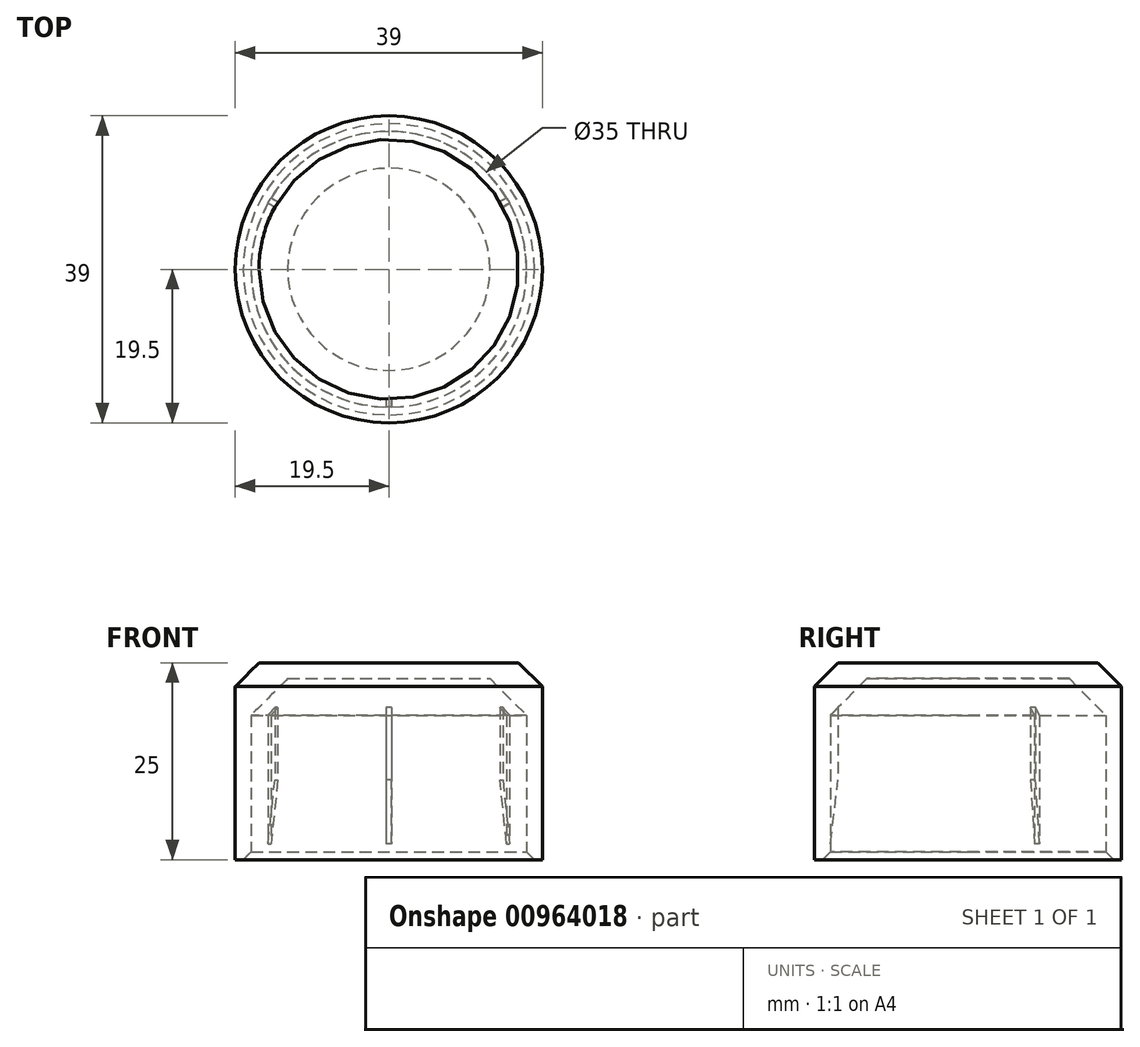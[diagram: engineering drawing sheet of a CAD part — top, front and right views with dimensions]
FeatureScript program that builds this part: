
annotation { "Feature Type Name" : "Feature", "Feature Type Description" : "" }
export const myFeature = defineFeature(function(context is Context, id is Id, definition is map)
    precondition{}
    {
        {
            var Q0;
            Q0=qCreatedBy(makeId("Front.planeOp"),FACE);
            var sketch = newSketch(context, id + "F0", { "sketchPlane" : qUnion([Q0])});
            skLineSegment(sketch, "E0", {"start": v(0, 0) * mm, "end": v(0, 33.94) * mm, "construction": true});
            skLineSegment(sketch, "E1", {"start": v(0, 25) * mm, "end": v(16.5, 25) * mm});
            skLineSegment(sketch, "E2", {"start": v(19.5, 22) * mm, "end": v(19.5, 0) * mm});
            skLineSegment(sketch, "E3", {"start": v(19.5, 0) * mm, "end": v(18.5, 0) * mm});
            skLineSegment(sketch, "E4", {"start": v(18.5, 0) * mm, "end": v(17.5, 1) * mm});
            skLineSegment(sketch, "E5", {"start": v(17.5, 1) * mm, "end": v(17.5, 18.34) * mm});
            skLineSegment(sketch, "E6", {"start": v(12.84, 23) * mm, "end": v(0, 23) * mm});
            skLineSegment(sketch, "E7", {"start": v(0, 23) * mm, "end": v(0, 25) * mm});
            skLineSegment(sketch, "E8", {"start": v(12.84, 23) * mm, "end": v(17.5, 18.34) * mm});
            skLineSegment(sketch, "E9", {"start": v(16.5, 25) * mm, "end": v(19.5, 22) * mm});
            skLineSegment(sketch, "E10", {"start": v(17.5, 1) * mm, "end": v(19.5, 1) * mm, "construction": true});
            skSolve(sketch);
        }
        {
            var Q0;
            Q0 = qSketchRegion(id + "F0", true);
            var Q1;
            Q1=sQuery(id+"F0.wireOp",EDGE,"E0");
            revolve(context, id + "F1", {"surfaceOperationType" : NewSurfaceOperationType.NEW, "entities" : qUnion([Q0]), "axis" : qUnion([Q1]), "revolveType" : RevolveType.FULL});
        }
        {
            var Q0;
            Q0=qCreatedBy(makeId("Top.planeOp"),FACE);
            cPlane(context, id + "F2", {"entities" : qUnion([Q0]), "cplaneType" : CPlaneType.OFFSET, "offset" : 2 * mm, "width" : 150 * mm, "height" : 150 * mm});
        }
        {
            var Q0;
            Q0=qCreatedBy(id+"F2.planeOp",FACE);
            var sketch = newSketch(context, id + "F3", { "sketchPlane" : qUnion([Q0])});
            skLineSegment(sketch, "E11.bottom", {"start": v(-0.38, -18.5) * mm, "end": v(0.38, -18.5) * mm});
            skLineSegment(sketch, "E11.top", {"start": v(-0.38, -16.5) * mm, "end": v(0.38, -16.5) * mm});
            skLineSegment(sketch, "E11.left", {"start": v(-0.38, -18.5) * mm, "end": v(-0.38, -16.5) * mm});
            skLineSegment(sketch, "E11.right", {"start": v(0.38, -18.5) * mm, "end": v(0.38, -16.5) * mm});
            skLineSegment(sketch, "E12.1.0", {"start": v(15.83, 9.57) * mm, "end": v(14.1, 8.57) * mm});
            skLineSegment(sketch, "E12.1.1", {"start": v(16.2, 8.92) * mm, "end": v(14.48, 7.93) * mm});
            skLineSegment(sketch, "E12.1.2", {"start": v(14.48, 7.93) * mm, "end": v(14.1, 8.57) * mm});
            skLineSegment(sketch, "E12.1.3", {"start": v(16.2, 8.92) * mm, "end": v(15.83, 9.57) * mm});
            skLineSegment(sketch, "E12.2.0", {"start": v(-16.2, 8.92) * mm, "end": v(-14.48, 7.93) * mm});
            skLineSegment(sketch, "E12.2.1", {"start": v(-15.83, 9.57) * mm, "end": v(-14.1, 8.57) * mm});
            skLineSegment(sketch, "E12.2.2", {"start": v(-14.1, 8.57) * mm, "end": v(-14.48, 7.93) * mm});
            skLineSegment(sketch, "E12.2.3", {"start": v(-15.83, 9.57) * mm, "end": v(-16.2, 8.92) * mm});
            skPoint(sketch, "E12.center", {"position": v(0, 0) * mm});
            skSolve(sketch);
        }
        {
            var Q0;
            Q0 = qSketchRegion(id + "F3", true);
            extrude(context, id + "F4", {"entities" : qUnion([Q0]), "operationType" : NewBodyOperationType.ADD, "endBound" : BoundingType.UP_TO_NEXT, "depth" : 15 * mm, "offsetDistance" : 25 * mm});
        }
        {
            var Q0;
            Q0=makeQuery(id+"F4.opExtrude","CAP_EDGE",EDGE,{"disambiguationData":[OSD([sQuery(id+"F3.wireOp",EDGE,"E11.top")])],"isStart":true});
            var Q1;
            Q1=makeQuery(id+"F4.opExtrude","CAP_EDGE",EDGE,{"disambiguationData":[OSD([sQuery(id+"F3.wireOp",EDGE,"E12.1.2")])],"isStart":true});
            var Q2;
            Q2=makeQuery(id+"F4.opExtrude","CAP_EDGE",EDGE,{"disambiguationData":[OSD([sQuery(id+"F3.wireOp",EDGE,"E12.2.2")])],"isStart":true});
            chamfer(context, id + "F5", {"entities" : qUnion([Q0, Q1, Q2]), "chamferType" : ChamferType.OFFSET_ANGLE, "width" : 1 * mm, "oppositeDirection" : false, "angle" : 83 * degree, "tangentPropagation" : true});
        }
    });
